# Revit family: Troffer Light - Lens
name_source: partatom
category: Lighting Fixtures
revit_build: Autodesk Revit Architecture 2012 (Build: 20110210_1515)
units: mm (PartAtom-declared; Revit-internal decimal feet)

## types (10) — shared parameters
Assembly Code = D5020210
Ballast Number of Poles = 1
Color Filter = 16777215
Diffuser Material = Glass - White, High Luminance
Dimming Lamp Color Temperature Shift = <None>
Emit Shape Visible in Rendering = No
Lamp = T-12
Light Box Material = Metal - Chrome
Light Source Symbol Size = 2' - 0"
Load Classification = Lighting - Dwelling Unit

## per-type parameters (varying)
| type | Apparent Load | Ballast Voltage | Box Length | Box Width | Circle Diameter | Emit from Rectangle Length | Emit from Rectangle Width |
| 2'x4'(4 Lamp) - 120V | 160 VA | 120 V | 4' - 0" | 2' - 0" | 1' - 2 13/32" | 3' - 10" | 1' - 10" |
| 2'x4'(4 Lamp) - 277V | 160 VA | 277 V | 4' - 0" | 2' - 0" | 1' - 2 13/32" | 3' - 10" | 1' - 10" |
| 1'x4'(2 Lamp) - 120V | 80 VA | 120 V | 4' - 0" | 0' - 11 31/32" | 0' - 7 3/16" | 3' - 10" | 0' - 9 31/32" |
| 1'x4'(2 Lamp) - 277V | 80 VA | 277 V | 4' - 0" | 0' - 11 31/32" | 0' - 7 3/16" | 3' - 10" | 0' - 9 31/32" |
| 2'x2'(2 Lamp) - 120V | 40 VA | 120 V | 2' - 0" | 2' - 0" | 1' - 2 13/32" | 1' - 10" | 1' - 10" |
| 2'x2'(2 Lamp) - 277V | 40 VA | 277 V | 2' - 0" | 2' - 0" | 1' - 2 13/32" | 1' - 10" | 1' - 10" |
| 2'x2'(4 Lamp) - 120V | 80 VA | 120 V | 2' - 0" | 2' - 0" | 1' - 2 13/32" | 1' - 10" | 1' - 10" |
| 2'x2'(4 Lamp) - 277V | 80 VA | 277 V | 2' - 0" | 2' - 0" | 1' - 2 13/32" | 1' - 10" | 1' - 10" |
| 2'x4'(2 Lamp) - 120V | 80 VA | 120 V | 4' - 0" | 2' - 0" | 1' - 2 13/32" | 3' - 10" | 1' - 10" |
| 2'x4'(2 Lamp) - 277V | 80 VA | 277 V | 4' - 0" | 2' - 0" | 1' - 2 13/32" | 3' - 10" | 1' - 10" |

## geometry (parser evidence)
native form markers: Sweep x1
no freeform markers — native parametric forms only
